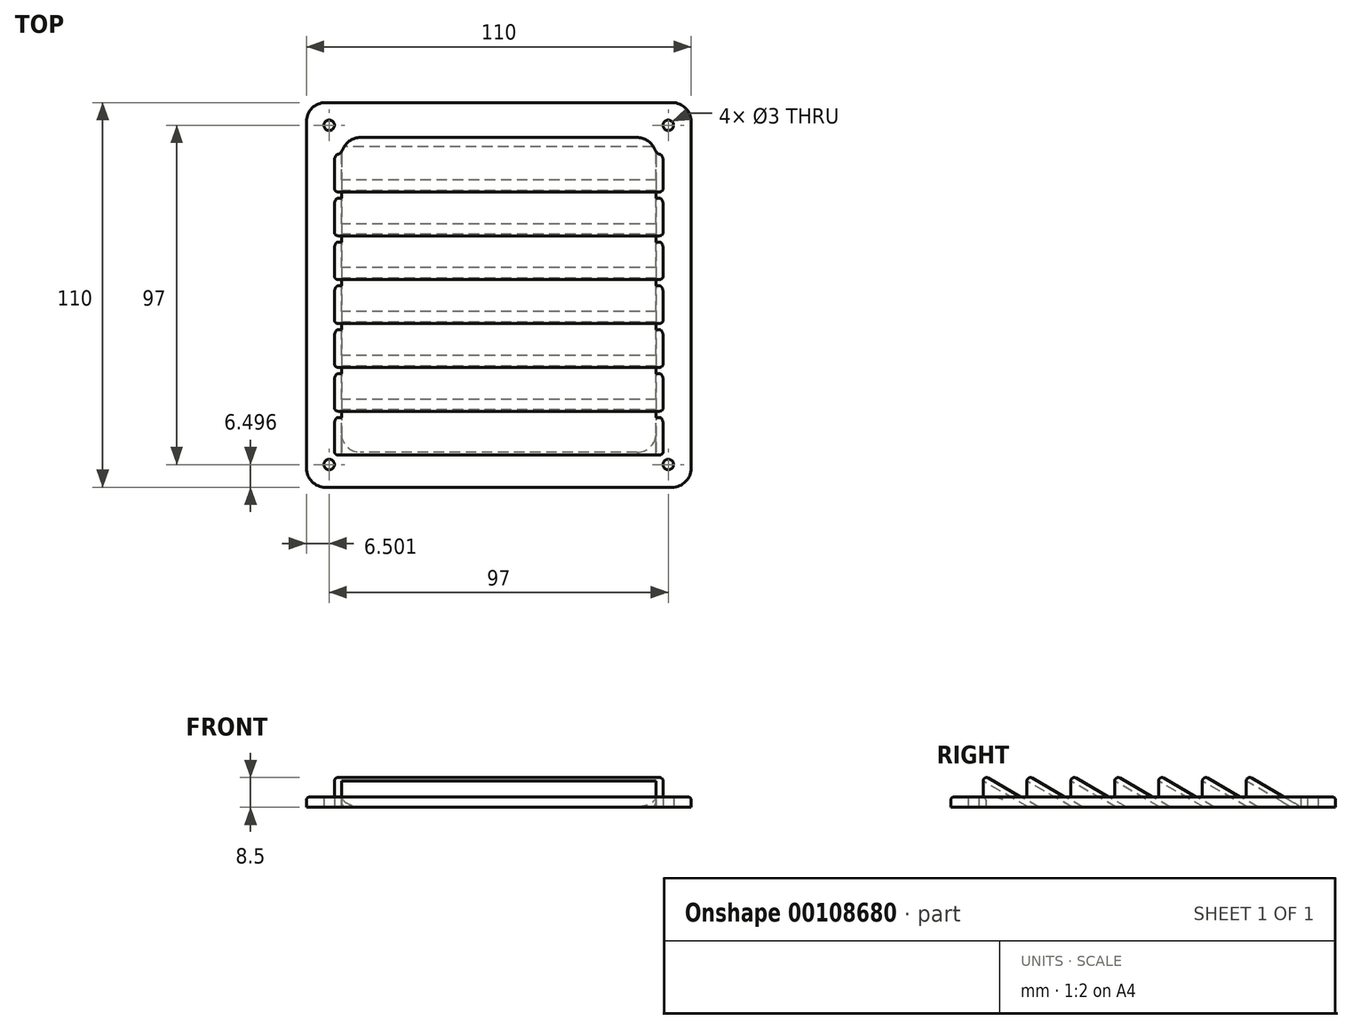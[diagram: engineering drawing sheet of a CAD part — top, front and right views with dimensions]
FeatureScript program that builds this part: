
annotation { "Feature Type Name" : "Feature", "Feature Type Description" : "" }
export const myFeature = defineFeature(function(context is Context, id is Id, definition is map)
    precondition{}
    {
        {
            var Q0;
            Q0=qCreatedBy(makeId("Top.planeOp"),FACE);
            var sketch = newSketch(context, id + "F0", { "sketchPlane" : qUnion([Q0])});
            skLineSegment(sketch, "E0.bottom", {"start": v(50.6, -52.71) * mm, "end": v(-48.53, -52.71) * mm});
            skLineSegment(sketch, "E0.top", {"start": v(50.6, 57.29) * mm, "end": v(-48.53, 57.29) * mm});
            skLineSegment(sketch, "E0.left", {"start": v(56.03, -47.27) * mm, "end": v(56.03, 51.85) * mm});
            skLineSegment(sketch, "E0.right", {"start": v(-53.97, -47.27) * mm, "end": v(-53.97, 51.85) * mm});
            skPoint(sketch, "E0.middle", {"position": v(1.03, 2.29) * mm});
            skLineSegment(sketch, "E1.bottom", {"start": v(40.6, -42.71) * mm, "end": v(-38.53, -42.71) * mm});
            skLineSegment(sketch, "E1.top", {"start": v(40.6, 47.29) * mm, "end": v(-38.53, 47.29) * mm});
            skLineSegment(sketch, "E1.left", {"start": v(46.03, -37.27) * mm, "end": v(46.03, 41.85) * mm});
            skLineSegment(sketch, "E1.right", {"start": v(-43.97, -37.27) * mm, "end": v(-43.97, 41.85) * mm});
            skPoint(sketch, "E2.visualSharp", {"position": v(-53.97, 57.29) * mm});
            skArc(sketch, "E2.filletArc", {"start": v(-48.53, 57.29) * mm, "mid": v(-52.38, 55.7) * mm, "end": v(-53.97, 51.85) * mm});
            skPoint(sketch, "E3.visualSharp", {"position": v(-43.97, 47.29) * mm});
            skArc(sketch, "E3.filletArc", {"start": v(-38.53, 47.29) * mm, "mid": v(-42.38, 45.7) * mm, "end": v(-43.97, 41.85) * mm});
            skPoint(sketch, "E4.visualSharp", {"position": v(46.03, 47.29) * mm});
            skArc(sketch, "E4.filletArc", {"start": v(46.03, 41.85) * mm, "mid": v(44.44, 45.7) * mm, "end": v(40.6, 47.29) * mm});
            skPoint(sketch, "E5.visualSharp", {"position": v(56.03, 57.29) * mm});
            skArc(sketch, "E5.filletArc", {"start": v(56.03, 51.85) * mm, "mid": v(54.44, 55.7) * mm, "end": v(50.6, 57.29) * mm});
            skPoint(sketch, "E6.visualSharp", {"position": v(56.03, -52.71) * mm});
            skArc(sketch, "E6.filletArc", {"start": v(50.6, -52.71) * mm, "mid": v(54.44, -51.12) * mm, "end": v(56.03, -47.27) * mm});
            skPoint(sketch, "E7.visualSharp", {"position": v(-53.97, -52.71) * mm});
            skArc(sketch, "E7.filletArc", {"start": v(-53.97, -47.27) * mm, "mid": v(-52.38, -51.12) * mm, "end": v(-48.53, -52.71) * mm});
            skPoint(sketch, "E8.visualSharp", {"position": v(-43.97, -42.71) * mm});
            skArc(sketch, "E8.filletArc", {"start": v(-43.97, -37.27) * mm, "mid": v(-42.38, -41.12) * mm, "end": v(-38.53, -42.71) * mm});
            skPoint(sketch, "E9.visualSharp", {"position": v(46.03, -42.71) * mm});
            skArc(sketch, "E9.filletArc", {"start": v(40.6, -42.71) * mm, "mid": v(44.44, -41.12) * mm, "end": v(46.03, -37.27) * mm});
            skCircle(sketch, "E10", {"center": v(-47.47, 50.79) * mm, "radius": 1.5 * mm});
            skCircle(sketch, "E11", {"center": v(49.53, 50.79) * mm, "radius": 1.5 * mm});
            skCircle(sketch, "E12", {"center": v(49.53, -46.21) * mm, "radius": 1.5 * mm});
            skCircle(sketch, "E13", {"center": v(-47.47, -46.21) * mm, "radius": 1.5 * mm});
            skSolve(sketch);
        }
        {
            var Q0;
            Q0 = qSketchRegion(id + "F0", true);
            extrude(context, id + "F1", {"entities" : qUnion([Q0]), "depth" : 3 * mm});
        }
        {
            var Q0;
            Q0=makeQuery(id+"F1.opExtrude","SWEPT_FACE",FACE,{"disambiguationData":[OSD([sQuery(id+"F0.wireOp",EDGE,"E1.right")])]});
            var sketch = newSketch(context, id + "F2", { "sketchPlane" : qUnion([Q0])});
            skLineSegment(sketch, "E14", {"start": v(-30.56, 0) * mm, "end": v(-27.56, 0) * mm});
            skLineSegment(sketch, "E15", {"start": v(-27.56, 0) * mm, "end": v(-43.5, 9.23) * mm});
            skLineSegment(sketch, "E16", {"start": v(-30.56, 0) * mm, "end": v(-43.5, 7.5) * mm});
            skPoint(sketch, "E17.start.orphan", {"position": v(-42.93, 0) * mm});
            skLineSegment(sketch, "E18", {"start": v(-43.5, 9.23) * mm, "end": v(-43.5, 7.5) * mm});
            skLineSegment(sketch, "E19.1.0.0", {"start": v(-30.97, 9.23) * mm, "end": v(-30.97, 7.5) * mm});
            skLineSegment(sketch, "E19.1.0.1", {"start": v(-18.02, 0) * mm, "end": v(-30.97, 7.5) * mm});
            skLineSegment(sketch, "E19.1.0.2", {"start": v(-15.02, 0) * mm, "end": v(-30.97, 9.23) * mm});
            skLineSegment(sketch, "E19.1.0.3", {"start": v(-18.02, 0) * mm, "end": v(-15.02, 0) * mm});
            skLineSegment(sketch, "E19.2.0.0", {"start": v(-18.43, 9.23) * mm, "end": v(-18.43, 7.5) * mm});
            skLineSegment(sketch, "E19.2.0.1", {"start": v(-5.47, 0) * mm, "end": v(-18.43, 7.5) * mm});
            skLineSegment(sketch, "E19.2.0.2", {"start": v(-2.47, 0) * mm, "end": v(-18.43, 9.23) * mm});
            skLineSegment(sketch, "E19.2.0.3", {"start": v(-5.47, 0) * mm, "end": v(-2.47, 0) * mm});
            skLineSegment(sketch, "E19.3.0.0", {"start": v(-5.88, 9.23) * mm, "end": v(-5.88, 7.5) * mm});
            skLineSegment(sketch, "E19.3.0.1", {"start": v(7.07, 0) * mm, "end": v(-5.88, 7.5) * mm});
            skLineSegment(sketch, "E19.3.0.2", {"start": v(10.07, 0) * mm, "end": v(-5.88, 9.23) * mm});
            skLineSegment(sketch, "E19.3.0.3", {"start": v(7.07, 0) * mm, "end": v(10.07, 0) * mm});
            skLineSegment(sketch, "E19.4.0.0", {"start": v(6.66, 9.23) * mm, "end": v(6.66, 7.5) * mm});
            skLineSegment(sketch, "E19.4.0.1", {"start": v(19.6, 0) * mm, "end": v(6.66, 7.5) * mm});
            skLineSegment(sketch, "E19.4.0.2", {"start": v(22.6, 0) * mm, "end": v(6.66, 9.23) * mm});
            skLineSegment(sketch, "E19.4.0.3", {"start": v(19.6, 0) * mm, "end": v(22.6, 0) * mm});
            skLineSegment(sketch, "E19.5.0.0", {"start": v(19.2, 9.23) * mm, "end": v(19.2, 7.5) * mm});
            skLineSegment(sketch, "E19.5.0.1", {"start": v(32.15, 0) * mm, "end": v(19.2, 7.5) * mm});
            skLineSegment(sketch, "E19.5.0.2", {"start": v(35.15, 0) * mm, "end": v(19.2, 9.23) * mm});
            skLineSegment(sketch, "E19.5.0.3", {"start": v(32.15, 0) * mm, "end": v(35.15, 0) * mm});
            skLineSegment(sketch, "E19.6.0.0", {"start": v(31.74, 9.23) * mm, "end": v(31.74, 7.5) * mm});
            skLineSegment(sketch, "E19.6.0.1", {"start": v(44.7, 0) * mm, "end": v(31.74, 7.5) * mm});
            skLineSegment(sketch, "E19.6.0.2", {"start": v(47.7, 0) * mm, "end": v(31.74, 9.23) * mm});
            skLineSegment(sketch, "E19.6.0.3", {"start": v(44.7, 0) * mm, "end": v(47.7, 0) * mm});
            skLineSegment(sketch, "E19.direction1", {"start": v(-43.5, 7.5) * mm, "end": v(-30.97, 7.5) * mm, "construction": true});
            skSolve(sketch);
        }
        {
            var Q0;
            Q0 = qSketchRegion(id + "F2", true);
            extrude(context, id + "F3", {"entities" : qUnion([Q0]), "operationType" : NewBodyOperationType.ADD, "depth" : 90 * mm});
        }
        {
            var Q0;
            Q0=makeQuery(id+"F3.opExtrude","CAP_FACE",FACE,{"disambiguationData":[OSD([sQuery(id+"F2.wireOp",EDGE,"E19.6.0.0"),sQuery(id+"F2.wireOp",EDGE,"E19.6.0.1"),sQuery(id+"F2.wireOp",EDGE,"E19.6.0.2"),sQuery(id+"F2.wireOp",EDGE,"E19.6.0.3")])],"isStart":true});
            var sketch = newSketch(context, id + "F4", { "sketchPlane" : qUnion([Q0])});
            skLineSegment(sketch, "E20", {"start": v(-31.74, 9.23) * mm, "end": v(-31.74, 3) * mm});
            skPoint(sketch, "E20.endSnap0", {"position": v(-31.74, 8.36) * mm});
            skLineSegment(sketch, "E21", {"start": v(-31.74, 3) * mm, "end": v(-42.5, 3) * mm});
            skLineSegment(sketch, "E22", {"start": v(-42.5, 3) * mm, "end": v(-31.74, 9.23) * mm});
            skLineSegment(sketch, "E23", {"start": v(-19.2, 9.23) * mm, "end": v(-19.2, 3) * mm});
            skLineSegment(sketch, "E24", {"start": v(-19.2, 3) * mm, "end": v(-29.97, 3) * mm});
            skLineSegment(sketch, "E25", {"start": v(-29.97, 3) * mm, "end": v(-19.2, 9.23) * mm});
            skLineSegment(sketch, "E26", {"start": v(-6.66, 9.23) * mm, "end": v(-6.66, 3) * mm});
            skLineSegment(sketch, "E27", {"start": v(-6.66, 3) * mm, "end": v(-17.42, 3) * mm});
            skLineSegment(sketch, "E28", {"start": v(-17.42, 3) * mm, "end": v(-6.66, 9.23) * mm});
            skLineSegment(sketch, "E29", {"start": v(5.88, 9.23) * mm, "end": v(5.88, 3) * mm});
            skLineSegment(sketch, "E30", {"start": v(5.88, 3) * mm, "end": v(-4.88, 3) * mm});
            skLineSegment(sketch, "E31", {"start": v(-4.88, 3) * mm, "end": v(5.88, 9.23) * mm});
            skLineSegment(sketch, "E32", {"start": v(18.43, 9.23) * mm, "end": v(18.43, 3) * mm});
            skLineSegment(sketch, "E33", {"start": v(18.43, 3) * mm, "end": v(7.66, 3) * mm});
            skLineSegment(sketch, "E34", {"start": v(7.66, 3) * mm, "end": v(18.43, 9.23) * mm});
            skLineSegment(sketch, "E35", {"start": v(30.97, 9.23) * mm, "end": v(30.97, 3) * mm});
            skLineSegment(sketch, "E36", {"start": v(30.97, 3) * mm, "end": v(20.2, 3) * mm});
            skLineSegment(sketch, "E37", {"start": v(20.2, 3) * mm, "end": v(30.97, 9.23) * mm});
            skLineSegment(sketch, "E38", {"start": v(43.5, 9.23) * mm, "end": v(43.5, 3) * mm});
            skLineSegment(sketch, "E39", {"start": v(43.5, 3) * mm, "end": v(32.74, 3) * mm});
            skLineSegment(sketch, "E40", {"start": v(32.74, 3) * mm, "end": v(43.5, 9.23) * mm});
            skSolve(sketch);
        }
        {
            var Q0;
            Q0 = qSketchRegion(id + "F4", true);
            extrude(context, id + "F5", {"entities" : qUnion([Q0]), "operationType" : NewBodyOperationType.ADD, "depth" : 2 * mm});
        }
        {
            var Q0;
            Q0=makeQuery(id+"F3.opExtrude","CAP_FACE",FACE,{"disambiguationData":[OSD([sQuery(id+"F2.wireOp",EDGE,"E14"),sQuery(id+"F2.wireOp",EDGE,"E15"),sQuery(id+"F2.wireOp",EDGE,"E16"),sQuery(id+"F2.wireOp",EDGE,"E18")])],"isStart":false});
            var sketch = newSketch(context, id + "F6", { "sketchPlane" : qUnion([Q0])});
            skLineSegment(sketch, "E41", {"start": v(-43.5, 9.23) * mm, "end": v(-43.5, 3) * mm});
            skLineSegment(sketch, "E42", {"start": v(-43.5, 3) * mm, "end": v(-32.74, 3) * mm});
            skLineSegment(sketch, "E43", {"start": v(-32.74, 3) * mm, "end": v(-43.5, 9.23) * mm});
            skLineSegment(sketch, "E44", {"start": v(-30.97, 9.23) * mm, "end": v(-30.97, 3) * mm});
            skLineSegment(sketch, "E45", {"start": v(-30.97, 3) * mm, "end": v(-20.2, 3) * mm});
            skLineSegment(sketch, "E46", {"start": v(-20.2, 3) * mm, "end": v(-30.97, 9.23) * mm});
            skLineSegment(sketch, "E47", {"start": v(-18.43, 9.23) * mm, "end": v(-18.43, 3) * mm});
            skLineSegment(sketch, "E48", {"start": v(-18.43, 3) * mm, "end": v(-7.66, 3) * mm});
            skLineSegment(sketch, "E49", {"start": v(-7.66, 3) * mm, "end": v(-18.43, 9.23) * mm});
            skLineSegment(sketch, "E50", {"start": v(-5.88, 9.23) * mm, "end": v(-5.88, 3) * mm});
            skLineSegment(sketch, "E51", {"start": v(-5.88, 3) * mm, "end": v(4.88, 3) * mm});
            skLineSegment(sketch, "E52", {"start": v(4.88, 3) * mm, "end": v(-5.88, 9.23) * mm});
            skLineSegment(sketch, "E53", {"start": v(6.66, 9.23) * mm, "end": v(6.66, 3) * mm});
            skLineSegment(sketch, "E54", {"start": v(6.66, 3) * mm, "end": v(17.42, 3) * mm});
            skLineSegment(sketch, "E55", {"start": v(17.42, 3) * mm, "end": v(6.66, 9.23) * mm});
            skLineSegment(sketch, "E56", {"start": v(19.2, 9.23) * mm, "end": v(19.2, 3) * mm});
            skLineSegment(sketch, "E57", {"start": v(19.2, 3) * mm, "end": v(29.97, 3) * mm});
            skLineSegment(sketch, "E58", {"start": v(29.97, 3) * mm, "end": v(19.2, 9.23) * mm});
            skLineSegment(sketch, "E59", {"start": v(31.74, 9.23) * mm, "end": v(31.74, 3) * mm});
            skLineSegment(sketch, "E60", {"start": v(31.74, 3) * mm, "end": v(42.5, 3) * mm});
            skLineSegment(sketch, "E61", {"start": v(42.5, 3) * mm, "end": v(31.74, 9.23) * mm});
            skSolve(sketch);
        }
        {
            var Q0;
            Q0 = qSketchRegion(id + "F6", true);
            extrude(context, id + "F7", {"entities" : qUnion([Q0]), "operationType" : NewBodyOperationType.ADD, "depth" : 2 * mm});
        }
        {
            var Q0;
            Q0=makeQuery(id+"F5.opExtrude","CAP_EDGE",EDGE,{"disambiguationData":[OSD([sQuery(id+"F4.wireOp",EDGE,"E22")])],"isStart":false});
            var Q1;
            Q1=makeQuery(id+"F5.opExtrude","CAP_EDGE",EDGE,{"disambiguationData":[OSD([sQuery(id+"F4.wireOp",EDGE,"E20")])],"isStart":false});
            var Q2;
            Q2=makeQuery(id+"F5.opExtrude","SWEPT_EDGE",EDGE,{"disambiguationData":[OSD([sQuery(id+"F4.wireOp",EDGE,"E20"),sQuery(id+"F4.wireOp",EDGE,"E22")])]});
            var Q3;
            Q3=makeQuery(id+"F5.opExtrude","CAP_EDGE",EDGE,{"disambiguationData":[OSD([sQuery(id+"F4.wireOp",EDGE,"E25")])],"isStart":false});
            var Q4;
            Q4=makeQuery(id+"F5.opExtrude","CAP_EDGE",EDGE,{"disambiguationData":[OSD([sQuery(id+"F4.wireOp",EDGE,"E23")])],"isStart":false});
            var Q5;
            Q5=makeQuery(id+"F5.opExtrude","SWEPT_EDGE",EDGE,{"disambiguationData":[OSD([sQuery(id+"F4.wireOp",EDGE,"E23"),sQuery(id+"F4.wireOp",EDGE,"E25")])]});
            var Q6;
            Q6=makeQuery(id+"F5.opExtrude","CAP_EDGE",EDGE,{"disambiguationData":[OSD([sQuery(id+"F4.wireOp",EDGE,"E28")])],"isStart":false});
            var Q7;
            Q7=makeQuery(id+"F5.opExtrude","CAP_EDGE",EDGE,{"disambiguationData":[OSD([sQuery(id+"F4.wireOp",EDGE,"E26")])],"isStart":false});
            var Q8;
            Q8=makeQuery(id+"F5.opExtrude","SWEPT_EDGE",EDGE,{"disambiguationData":[OSD([sQuery(id+"F4.wireOp",EDGE,"E26"),sQuery(id+"F4.wireOp",EDGE,"E28")])]});
            var Q9;
            Q9=makeQuery(id+"F5.opExtrude","SWEPT_EDGE",EDGE,{"disambiguationData":[OSD([sQuery(id+"F4.wireOp",EDGE,"E32"),sQuery(id+"F4.wireOp",EDGE,"E34")])]});
            var Q10;
            Q10=makeQuery(id+"F5.opExtrude","CAP_EDGE",EDGE,{"disambiguationData":[OSD([sQuery(id+"F4.wireOp",EDGE,"E34")])],"isStart":false});
            var Q11;
            Q11=makeQuery(id+"F5.opExtrude","CAP_EDGE",EDGE,{"disambiguationData":[OSD([sQuery(id+"F4.wireOp",EDGE,"E32")])],"isStart":false});
            var Q12;
            Q12=makeQuery(id+"F5.opExtrude","CAP_EDGE",EDGE,{"disambiguationData":[OSD([sQuery(id+"F4.wireOp",EDGE,"E37")])],"isStart":false});
            var Q13;
            Q13=makeQuery(id+"F5.opExtrude","SWEPT_EDGE",EDGE,{"disambiguationData":[OSD([sQuery(id+"F4.wireOp",EDGE,"E35"),sQuery(id+"F4.wireOp",EDGE,"E37")])]});
            var Q14;
            Q14=makeQuery(id+"F5.opExtrude","CAP_EDGE",EDGE,{"disambiguationData":[OSD([sQuery(id+"F4.wireOp",EDGE,"E35")])],"isStart":false});
            var Q15;
            Q15=makeQuery(id+"F5.opExtrude","SWEPT_EDGE",EDGE,{"disambiguationData":[OSD([sQuery(id+"F4.wireOp",EDGE,"E38"),sQuery(id+"F4.wireOp",EDGE,"E40")])]});
            var Q16;
            Q16=makeQuery(id+"F5.opExtrude","CAP_EDGE",EDGE,{"disambiguationData":[OSD([sQuery(id+"F4.wireOp",EDGE,"E40")])],"isStart":false});
            var Q17;
            Q17=makeQuery(id+"F5.opExtrude","CAP_EDGE",EDGE,{"disambiguationData":[OSD([sQuery(id+"F4.wireOp",EDGE,"E38")])],"isStart":false});
            var Q18;
            Q18=makeQuery(id+"F1.opExtrude","CAP_EDGE",EDGE,{"disambiguationData":[OSD([sQuery(id+"F0.wireOp",EDGE,"E0.right")])],"isStart":false});
            var Q19;
            Q19=makeQuery(id+"F7.opExtrude","CAP_EDGE",EDGE,{"disambiguationData":[OSD([sQuery(id+"F6.wireOp",EDGE,"E43")])],"isStart":false});
            var Q20;
            Q20=makeQuery(id+"F7.opExtrude","CAP_EDGE",EDGE,{"disambiguationData":[OSD([sQuery(id+"F6.wireOp",EDGE,"E41")])],"isStart":false});
            var Q21;
            Q21=makeQuery(id+"F7.opExtrude","SWEPT_EDGE",EDGE,{"disambiguationData":[OSD([sQuery(id+"F6.wireOp",EDGE,"E41"),sQuery(id+"F6.wireOp",EDGE,"E43")])]});
            var Q22;
            Q22=makeQuery(id+"F7.opExtrude","CAP_EDGE",EDGE,{"disambiguationData":[OSD([sQuery(id+"F6.wireOp",EDGE,"E44")])],"isStart":false});
            var Q23;
            Q23=makeQuery(id+"F7.opExtrude","CAP_EDGE",EDGE,{"disambiguationData":[OSD([sQuery(id+"F6.wireOp",EDGE,"E46")])],"isStart":false});
            var Q24;
            Q24=makeQuery(id+"F7.opExtrude","SWEPT_EDGE",EDGE,{"disambiguationData":[OSD([sQuery(id+"F6.wireOp",EDGE,"E44"),sQuery(id+"F6.wireOp",EDGE,"E46")])]});
            var Q25;
            Q25=makeQuery(id+"F7.opExtrude","CAP_EDGE",EDGE,{"disambiguationData":[OSD([sQuery(id+"F6.wireOp",EDGE,"E47")])],"isStart":false});
            var Q26;
            Q26=makeQuery(id+"F7.opExtrude","CAP_EDGE",EDGE,{"disambiguationData":[OSD([sQuery(id+"F6.wireOp",EDGE,"E49")])],"isStart":false});
            var Q27;
            Q27=makeQuery(id+"F7.opExtrude","SWEPT_EDGE",EDGE,{"disambiguationData":[OSD([sQuery(id+"F6.wireOp",EDGE,"E47"),sQuery(id+"F6.wireOp",EDGE,"E49")])]});
            var Q28;
            Q28=makeQuery(id+"F7.opExtrude","CAP_EDGE",EDGE,{"disambiguationData":[OSD([sQuery(id+"F6.wireOp",EDGE,"E50")])],"isStart":false});
            var Q29;
            Q29=makeQuery(id+"F7.opExtrude","CAP_EDGE",EDGE,{"disambiguationData":[OSD([sQuery(id+"F6.wireOp",EDGE,"E52")])],"isStart":false});
            var Q30;
            Q30=makeQuery(id+"F7.opExtrude","SWEPT_EDGE",EDGE,{"disambiguationData":[OSD([sQuery(id+"F6.wireOp",EDGE,"E50"),sQuery(id+"F6.wireOp",EDGE,"E52")])]});
            var Q31;
            Q31=makeQuery(id+"F7.opExtrude","CAP_EDGE",EDGE,{"disambiguationData":[OSD([sQuery(id+"F6.wireOp",EDGE,"E53")])],"isStart":false});
            var Q32;
            Q32=makeQuery(id+"F7.opExtrude","CAP_EDGE",EDGE,{"disambiguationData":[OSD([sQuery(id+"F6.wireOp",EDGE,"E55")])],"isStart":false});
            var Q33;
            Q33=makeQuery(id+"F7.opExtrude","SWEPT_EDGE",EDGE,{"disambiguationData":[OSD([sQuery(id+"F6.wireOp",EDGE,"E53"),sQuery(id+"F6.wireOp",EDGE,"E55")])]});
            var Q34;
            Q34=makeQuery(id+"F7.opExtrude","CAP_EDGE",EDGE,{"disambiguationData":[OSD([sQuery(id+"F6.wireOp",EDGE,"E56")])],"isStart":false});
            var Q35;
            Q35=makeQuery(id+"F7.opExtrude","CAP_EDGE",EDGE,{"disambiguationData":[OSD([sQuery(id+"F6.wireOp",EDGE,"E58")])],"isStart":false});
            var Q36;
            Q36=makeQuery(id+"F7.opExtrude","SWEPT_EDGE",EDGE,{"disambiguationData":[OSD([sQuery(id+"F6.wireOp",EDGE,"E56"),sQuery(id+"F6.wireOp",EDGE,"E58")])]});
            var Q37;
            Q37=makeQuery(id+"F7.opExtrude","CAP_EDGE",EDGE,{"disambiguationData":[OSD([sQuery(id+"F6.wireOp",EDGE,"E59")])],"isStart":false});
            var Q38;
            Q38=makeQuery(id+"F7.opExtrude","CAP_EDGE",EDGE,{"disambiguationData":[OSD([sQuery(id+"F6.wireOp",EDGE,"E61")])],"isStart":false});
            var Q39;
            Q39=makeQuery(id+"F7.opExtrude","SWEPT_EDGE",EDGE,{"disambiguationData":[OSD([sQuery(id+"F6.wireOp",EDGE,"E59"),sQuery(id+"F6.wireOp",EDGE,"E61")])]});
            var Q40;
            Q40=makeQuery(id+"F3.opExtrude","SWEPT_EDGE",EDGE,{"disambiguationData":[OSD([sQuery(id+"F2.wireOp",EDGE,"E19.6.0.0"),sQuery(id+"F2.wireOp",EDGE,"E19.6.0.2")])]});
            var Q41;
            Q41=makeQuery(id+"F3.opExtrude","SWEPT_EDGE",EDGE,{"disambiguationData":[OSD([sQuery(id+"F2.wireOp",EDGE,"E19.5.0.0"),sQuery(id+"F2.wireOp",EDGE,"E19.5.0.2")])]});
            var Q42;
            Q42=makeQuery(id+"F3.opExtrude","SWEPT_EDGE",EDGE,{"disambiguationData":[OSD([sQuery(id+"F2.wireOp",EDGE,"E19.4.0.0"),sQuery(id+"F2.wireOp",EDGE,"E19.4.0.2")])]});
            var Q43;
            Q43=makeQuery(id+"F3.opExtrude","SWEPT_EDGE",EDGE,{"disambiguationData":[OSD([sQuery(id+"F2.wireOp",EDGE,"E19.3.0.0"),sQuery(id+"F2.wireOp",EDGE,"E19.3.0.2")])]});
            var Q44;
            Q44=makeQuery(id+"F3.opExtrude","SWEPT_EDGE",EDGE,{"disambiguationData":[OSD([sQuery(id+"F2.wireOp",EDGE,"E19.2.0.0"),sQuery(id+"F2.wireOp",EDGE,"E19.2.0.2")])]});
            var Q45;
            Q45=makeQuery(id+"F3.opExtrude","SWEPT_EDGE",EDGE,{"disambiguationData":[OSD([sQuery(id+"F2.wireOp",EDGE,"E19.1.0.0"),sQuery(id+"F2.wireOp",EDGE,"E19.1.0.2")])]});
            var Q46;
            Q46=makeQuery(id+"F3.opExtrude","SWEPT_EDGE",EDGE,{"disambiguationData":[OSD([sQuery(id+"F2.wireOp",EDGE,"E15"),sQuery(id+"F2.wireOp",EDGE,"E18")])]});
            var Q47;
            Q47=makeQuery(id+"F5.opExtrude","CAP_EDGE",EDGE,{"disambiguationData":[OSD([sQuery(id+"F4.wireOp",EDGE,"E31")])],"isStart":false});
            var Q48;
            Q48=makeQuery(id+"F5.opExtrude","CAP_EDGE",EDGE,{"disambiguationData":[OSD([sQuery(id+"F4.wireOp",EDGE,"E29")])],"isStart":false});
            var Q49;
            Q49=makeQuery(id+"F5.opExtrude","SWEPT_EDGE",EDGE,{"disambiguationData":[OSD([sQuery(id+"F4.wireOp",EDGE,"E29"),sQuery(id+"F4.wireOp",EDGE,"E31")])]});
            var Q50;
            Q50=makeQuery(id+"F1.opExtrude","CAP_EDGE",EDGE,{"disambiguationData":[OSD([sQuery(id+"F0.wireOp",EDGE,"E1.top")])],"isStart":false});
            var Q51;
            Q51=makeQuery(id+"F1.opExtrude","CAP_EDGE",EDGE,{"disambiguationData":[OSD([sQuery(id+"F0.wireOp",EDGE,"E1.bottom")])],"isStart":false});
            fillet(context, id + "F8", {"entities" : qUnion([Q0, Q1, Q2, Q3, Q4, Q5, Q6, Q7, Q8, Q9, Q10, Q11, Q12, Q13, Q14, Q15, Q16, Q17, Q18, Q19, Q20, Q21, Q22, Q23, Q24, Q25, Q26, Q27, Q28, Q29, Q30, Q31, Q32, Q33, Q34, Q35, Q36, Q37, Q38, Q39, Q40, Q41, Q42, Q43, Q44, Q45, Q46, Q47, Q48, Q49, Q50, Q51]), "radius" : 1 * mm, "tangentPropagation" : true, "allowEdgeOverflow" : false});
        }
    });
